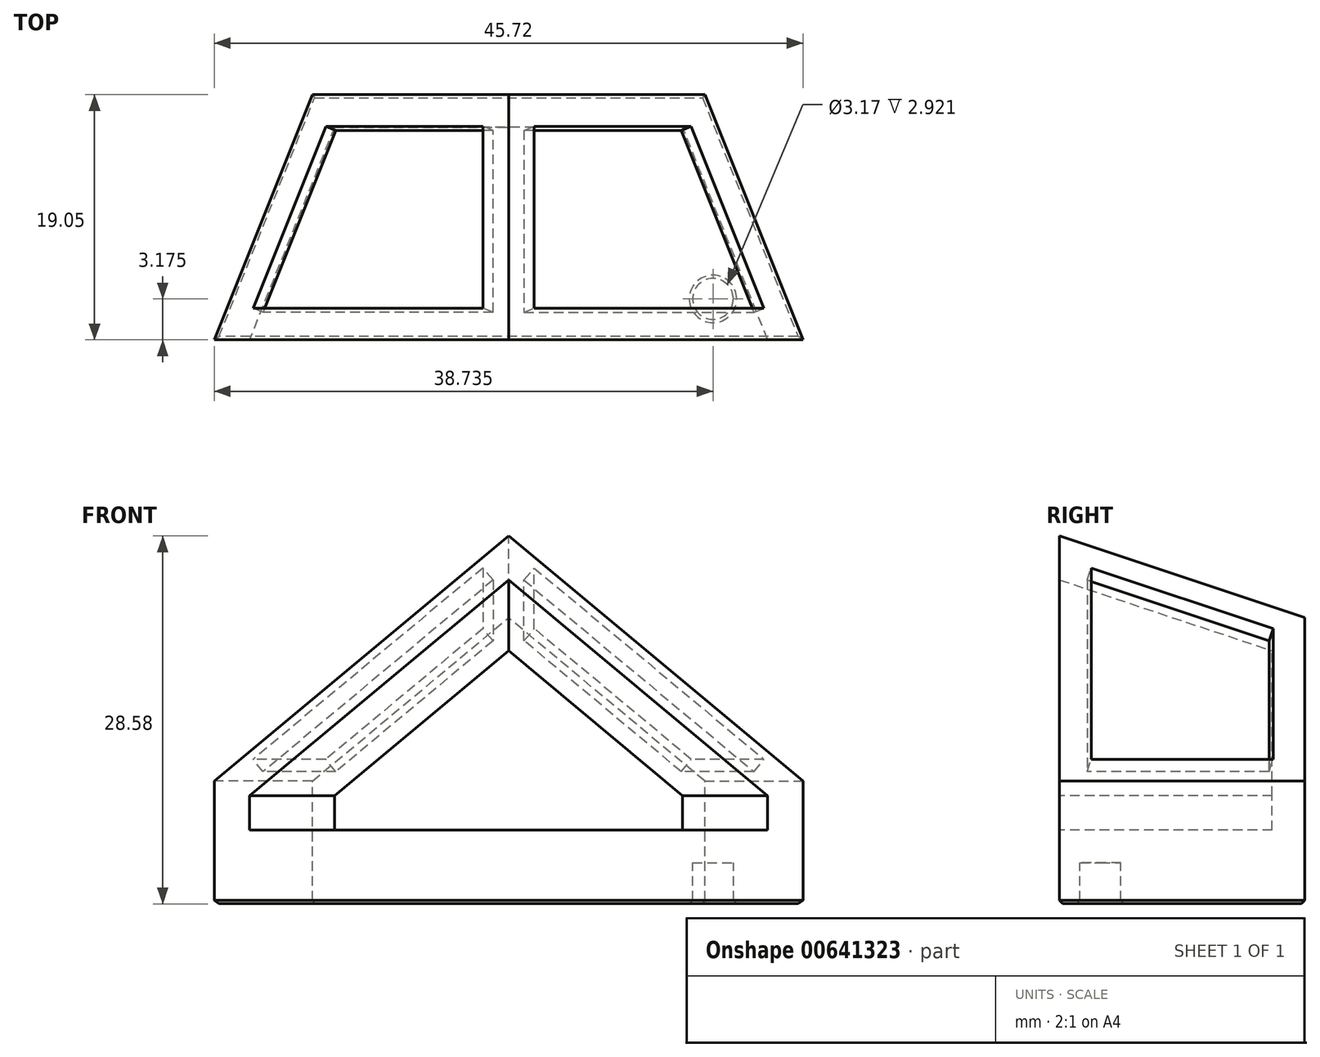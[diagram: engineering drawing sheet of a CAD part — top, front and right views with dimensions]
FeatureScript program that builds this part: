
annotation { "Feature Type Name" : "Feature", "Feature Type Description" : "" }
export const myFeature = defineFeature(function(context is Context, id is Id, definition is map)
    precondition{}
    {
        {
            var Q0;
            Q0=qCreatedBy(makeId("Front.planeOp"),FACE);
            var sketch = newSketch(context, id + "F0", { "sketchPlane" : qUnion([Q0])});
            skLineSegment(sketch, "E0", {"start": v(0, 0) * mm, "end": v(15.24, 0) * mm});
            skLineSegment(sketch, "E1", {"start": v(15.24, 0) * mm, "end": v(15.24, 6.35) * mm});
            skLineSegment(sketch, "E2", {"start": v(15.24, 6.35) * mm, "end": v(0, 19.05) * mm});
            skLineSegment(sketch, "E3.MirrorCS", {"start": v(-15.24, 6.35) * mm, "end": v(0, 19.05) * mm});
            skLineSegment(sketch, "E4.MirrorCS", {"start": v(-15.24, 0) * mm, "end": v(-15.24, 6.35) * mm});
            skLineSegment(sketch, "E5.MirrorCS", {"start": v(0, 0) * mm, "end": v(-15.24, 0) * mm});
            skSolve(sketch);
        }
        {
            var Q0;
            Q0=qCreatedBy(makeId("Front.planeOp"),FACE);
            cPlane(context, id + "F1", {"entities" : qUnion([Q0]), "cplaneType" : CPlaneType.OFFSET, "offset" : 19.05 * mm, "width" : 152.4 * mm, "height" : 152.4 * mm});
        }
        {
            var Q0;
            Q0=qCreatedBy(id+"F1.planeOp",FACE);
            var sketch = newSketch(context, id + "F2", { "sketchPlane" : qUnion([Q0])});
            skLineSegment(sketch, "E6", {"start": v(0, 0) * mm, "end": v(22.86, 0) * mm});
            skLineSegment(sketch, "E7", {"start": v(22.86, 0) * mm, "end": v(22.86, 6.35) * mm});
            skLineSegment(sketch, "E8", {"start": v(22.86, 6.35) * mm, "end": v(0, 25.4) * mm});
            skLineSegment(sketch, "E9.MirrorCS", {"start": v(-22.86, 6.35) * mm, "end": v(0, 25.4) * mm});
            skLineSegment(sketch, "E10.MirrorCS", {"start": v(-22.86, 0) * mm, "end": v(-22.86, 6.35) * mm});
            skLineSegment(sketch, "E11.MirrorCS", {"start": v(0, 0) * mm, "end": v(-22.86, 0) * mm});
            skSolve(sketch);
        }
        {
            var Q0;
            Q0=makeQuery(id+"F0.imprint","IMPRINT",FACE,{"disambiguationData":[TD([[makeQuery(id+"F0.imprint","IMPRINT",EDGE,{"derivedFrom":sQuery(id+"F0.wireOp",EDGE,"E0")}),1.0]])]});
            var Q1;
            Q1=makeQuery(id+"F2.imprint","IMPRINT",FACE,{"disambiguationData":[TD([[makeQuery(id+"F2.imprint","IMPRINT",EDGE,{"derivedFrom":sQuery(id+"F2.wireOp",EDGE,"E6")}),1.0]])]});
            loft(context, id + "F3", {"sheetProfilesArray" : [{ "sheetProfileEntities" : qUnion([Q0]) }, { "sheetProfileEntities" : qUnion([Q1]) }]});
        }
        {
            var Q0;
            Q0=makeQuery(id+"F3.opLoft","SWEPT_FACE",FACE,{"disambiguationData":[OSD([sQuery(id+"F0.wireOp",EDGE,"E2"),sQuery(id+"F0.wireOp",EDGE,"E3.MirrorCS"),sQuery(id+"F0.wireOp",EDGE,"E4.MirrorCS"),sQuery(id+"F2.wireOp",EDGE,"E8"),sQuery(id+"F2.wireOp",EDGE,"E9.MirrorCS"),sQuery(id+"F2.wireOp",EDGE,"E10.MirrorCS")])]});
            var sketch = newSketch(context, id + "F4", { "sketchPlane" : qUnion([Q0])});
            skLineSegment(sketch, "E12.0", {"start": v(-6.88, -4.88) * mm, "end": v(-14.08, -18.28) * mm});
            skLineSegment(sketch, "E12.1", {"start": v(8.67, -8.1) * mm, "end": v(-6.88, -4.88) * mm});
            skLineSegment(sketch, "E12.2", {"start": v(8.67, -22.99) * mm, "end": v(8.67, -8.1) * mm});
            skLineSegment(sketch, "E12.3", {"start": v(8.67, -22.99) * mm, "end": v(-14.08, -18.28) * mm});
            skSolve(sketch);
        }
        {
            var Q0;
            Q0=makeQuery(id+"F3.opLoft","SWEPT_FACE",FACE,{"disambiguationData":[OSD([sQuery(id+"F0.wireOp",EDGE,"E1"),sQuery(id+"F0.wireOp",EDGE,"E2"),sQuery(id+"F0.wireOp",EDGE,"E3.MirrorCS"),sQuery(id+"F2.wireOp",EDGE,"E7"),sQuery(id+"F2.wireOp",EDGE,"E8"),sQuery(id+"F2.wireOp",EDGE,"E9.MirrorCS")])]});
            var sketch = newSketch(context, id + "F5", { "sketchPlane" : qUnion([Q0])});
            skLineSegment(sketch, "E13.0", {"start": v(-8.67, -8.1) * mm, "end": v(-8.67, -22.99) * mm});
            skLineSegment(sketch, "E13.1", {"start": v(6.88, -4.88) * mm, "end": v(-8.67, -8.1) * mm});
            skLineSegment(sketch, "E13.2", {"start": v(14.08, -18.28) * mm, "end": v(6.88, -4.88) * mm});
            skLineSegment(sketch, "E13.3", {"start": v(-8.67, -22.99) * mm, "end": v(14.08, -18.28) * mm});
            skSolve(sketch);
        }
        {
            var Q0;
            Q0=makeQuery(id+"F3.opLoft","CAP_FACE",FACE,{"disambiguationData":[OSD([makeQuery(id+"F2.imprint","IMPRINT",FACE,{"disambiguationData":[TD([[makeQuery(id+"F2.imprint","IMPRINT",EDGE,{"derivedFrom":sQuery(id+"F2.wireOp",EDGE,"E6")}),1.0]])]})])],"isStart":true});
            shell(context, id + "F6", {"entities" : qUnion([Q0]), "thickness" : 2.54 * mm});
        }
        {
            var Q0;
            Q0=makeQuery(id+"F4.imprint","IMPRINT",FACE,{"disambiguationData":[TD([[makeQuery(id+"F4.imprint","IMPRINT",EDGE,{"derivedFrom":sQuery(id+"F4.wireOp",EDGE,"E12.0")}),1.0]])]});
            extrude(context, id + "F7", {"entities" : qUnion([Q0]), "operationType" : NewBodyOperationType.REMOVE, "oppositeDirection" : true, "depth" : 1.27 * mm, "offsetDistance" : 25.4 * mm});
        }
        {
            var Q0;
            Q0=makeQuery(id+"F5.imprint","IMPRINT",FACE,{"disambiguationData":[TD([[makeQuery(id+"F5.imprint","IMPRINT",EDGE,{"derivedFrom":sQuery(id+"F5.wireOp",EDGE,"E13.0")}),1.0]])]});
            extrude(context, id + "F8", {"entities" : qUnion([Q0]), "operationType" : NewBodyOperationType.REMOVE, "oppositeDirection" : true, "depth" : 1.27 * mm, "offsetDistance" : 25.4 * mm});
        }
        {
            var Q0;
            Q0=makeQuery(id+"F3.opLoft","SWEPT_FACE",FACE,{"disambiguationData":[OSD([sQuery(id+"F0.wireOp",EDGE,"E0"),sQuery(id+"F0.wireOp",EDGE,"E4.MirrorCS"),sQuery(id+"F0.wireOp",EDGE,"E5.MirrorCS"),sQuery(id+"F2.wireOp",EDGE,"E6"),sQuery(id+"F2.wireOp",EDGE,"E10.MirrorCS"),sQuery(id+"F2.wireOp",EDGE,"E11.MirrorCS")])]});
            var sketch = newSketch(context, id + "F9", { "sketchPlane" : qUnion([Q0])});
            skLineSegment(sketch, "E14", {"start": v(0, 0) * mm, "end": v(0, 3.18) * mm});
            skCircle(sketch, "E15", {"center": v(0, 3.18) * mm, "radius": 1.59 * mm});
            skLineSegment(sketch, "E16", {"start": v(0, 3.18) * mm, "end": v(0, 15.88) * mm});
            skLineSegment(sketch, "E17", {"start": v(0, 15.88) * mm, "end": v(-15.88, 15.88) * mm});
            skCircle(sketch, "E18", {"center": v(-15.88, 15.88) * mm, "radius": 1.59 * mm});
            skCircle(sketch, "E19.MirrorC", {"center": v(15.88, 15.88) * mm, "radius": 1.59 * mm});
            skSolve(sketch);
        }
        {
            var Q0;
            Q0=makeQuery(id+"F9.imprint","IMPRINT",FACE,{"disambiguationData":[TD([[makeQuery(id+"F9.imprint","IMPRINT",EDGE,{"derivedFrom":sQuery(id+"F9.wireOp",EDGE,"E18")}),1.0]])]});
            var Q1;
            Q1=makeQuery(id+"F9.imprint","IMPRINT",FACE,{"disambiguationData":[TD([[makeQuery(id+"F9.imprint","IMPRINT",EDGE,{"derivedFrom":sQuery(id+"F9.wireOp",EDGE,"E19.MirrorC")}),-1.0]])]});
            var Q2;
            {var subQ0=sQuery(id+"F9.wireOp",EDGE,"E16");var subQ1=sQuery(id+"F9.wireOp",EDGE,"E14");var subQ2=makeQuery(id+"F9.imprint","INTERSECT",VERTEX,{"derivedFrom":[subQ1,subQ0]});Q2=makeQuery(id+"F9.imprint","IMPRINT",FACE,{"disambiguationData":[TD([[makeQuery(id+"F9.imprint","IMPRINT",EDGE,{"disambiguationData":[TD([[subQ2,1.0]])],"derivedFrom":subQ1}),1.0]])]});}
            var Q3;
            {var subQ0=sQuery(id+"F9.wireOp",EDGE,"E16");var subQ1=sQuery(id+"F9.wireOp",EDGE,"E14");var subQ2=makeQuery(id+"F9.imprint","INTERSECT",VERTEX,{"derivedFrom":[subQ1,subQ0]});Q3=makeQuery(id+"F9.imprint","IMPRINT",FACE,{"disambiguationData":[TD([[makeQuery(id+"F9.imprint","IMPRINT",EDGE,{"disambiguationData":[TD([[subQ2,1.0]])],"derivedFrom":subQ1}),-1.0]])]});}
            extrude(context, id + "F10", {"entities" : qUnion([Q0, Q1, Q2, Q3]), "operationType" : NewBodyOperationType.ADD, "depth" : 3.17 * mm, "offsetDistance" : 25.4 * mm});
        }
        {
            var Q0;
            Q0=makeQuery(id+"F10.opExtrude","CAP_FACE",FACE,{"disambiguationData":[OSD([sQuery(id+"F9.wireOp",EDGE,"E18")])],"isStart":false});
            var Q1;
            Q1=makeQuery(id+"F10.opExtrude","CAP_FACE",FACE,{"disambiguationData":[OSD([sQuery(id+"F9.wireOp",EDGE,"E19.MirrorC")])],"isStart":false});
            var Q2;
            Q2=makeQuery(id+"F10.opExtrude","CAP_EDGE",EDGE,{"disambiguationData":[OSD([sQuery(id+"F9.wireOp",EDGE,"E15")])],"isStart":false});
            chamfer(context, id + "F11", {"entities" : qUnion([Q0, Q1, Q2]), "chamferType" : ChamferType.OFFSET_ANGLE, "width" : 0.25 * mm, "oppositeDirection" : false, "angle" : 45 * degree, "tangentPropagation" : true});
        }
    });
